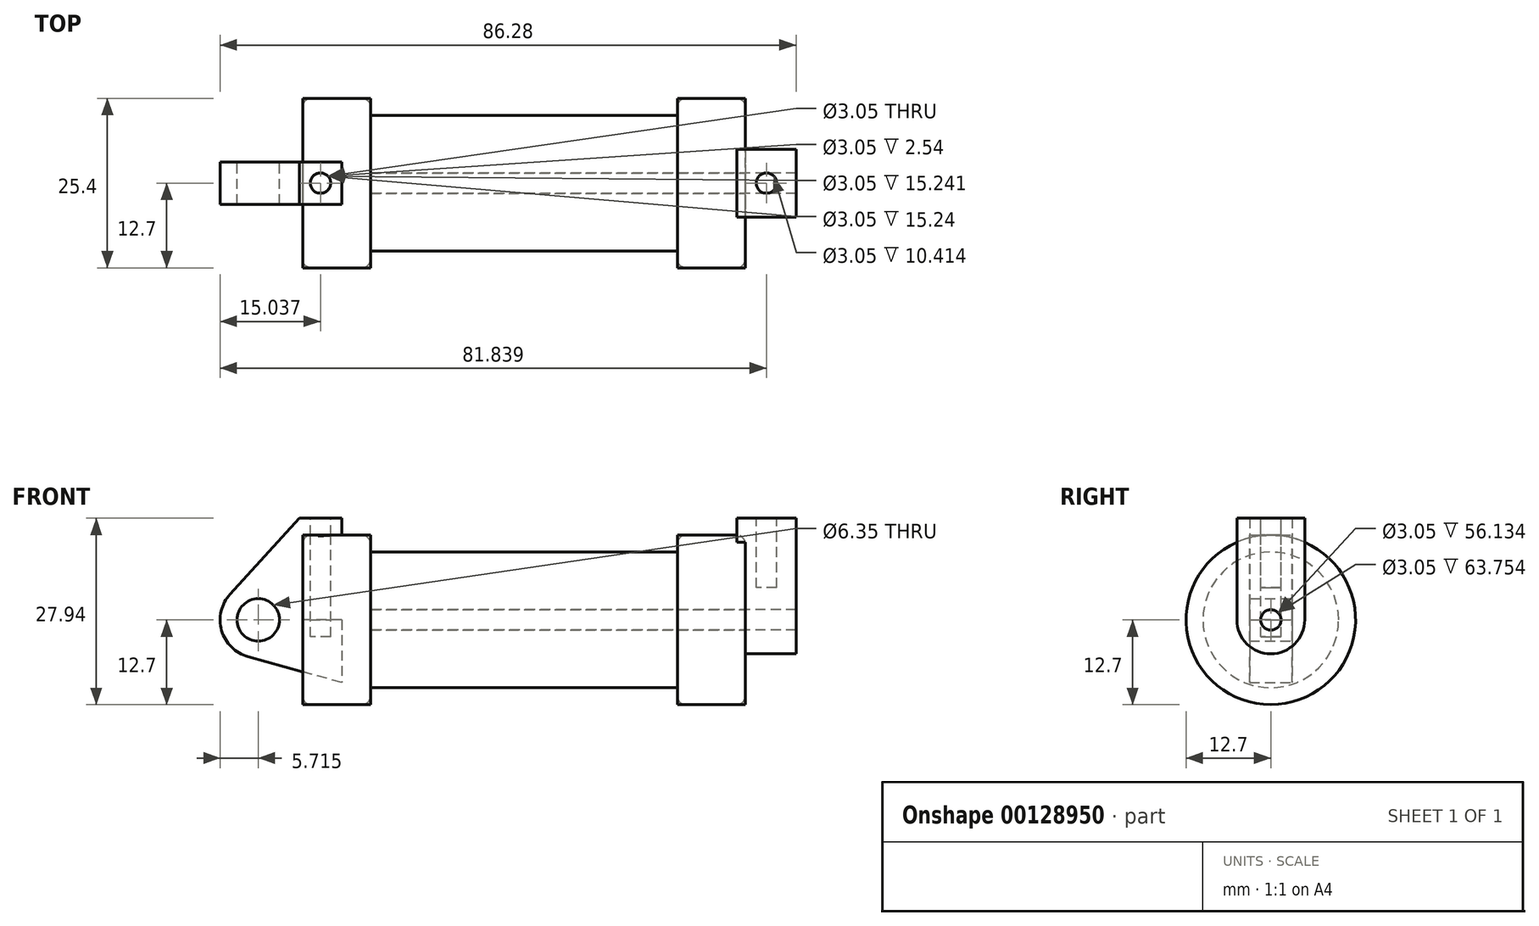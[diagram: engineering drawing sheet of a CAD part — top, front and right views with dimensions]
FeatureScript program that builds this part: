
annotation { "Feature Type Name" : "Feature", "Feature Type Description" : "" }
export const myFeature = defineFeature(function(context is Context, id is Id, definition is map)
    precondition{}
    {
        {
            var Q0;
            Q0=qCreatedBy(makeId("Front.planeOp"),FACE);
            var sketch = newSketch(context, id + "F0", { "sketchPlane" : qUnion([Q0])});
            skLineSegment(sketch, "E0", {"start": v(0, 0) * mm, "end": v(0, 12.7) * mm});
            skLineSegment(sketch, "E1", {"start": v(0, 12.7) * mm, "end": v(10.16, 12.7) * mm});
            skLineSegment(sketch, "E2", {"start": v(10.16, 12.7) * mm, "end": v(10.16, 10.16) * mm});
            skLineSegment(sketch, "E3", {"start": v(10.16, 10.16) * mm, "end": v(56.13, 10.16) * mm});
            skLineSegment(sketch, "E4", {"start": v(56.13, 10.16) * mm, "end": v(56.13, 12.7) * mm});
            skLineSegment(sketch, "E5", {"start": v(56.13, 12.7) * mm, "end": v(66.3, 12.7) * mm});
            skLineSegment(sketch, "E6", {"start": v(66.3, 12.7) * mm, "end": v(66.3, 0) * mm});
            skLineSegment(sketch, "E7", {"start": v(66.3, 0) * mm, "end": v(0, 0) * mm});
            skLineSegment(sketch, "E8", {"start": v(5.84, 15.24) * mm, "end": v(-0.5, 15.24) * mm});
            skLineSegment(sketch, "E9", {"start": v(-0.5, 15.24) * mm, "end": v(-10.88, 3.85) * mm});
            skLineSegment(sketch, "E10", {"start": v(0, 0) * mm, "end": v(-6.65, 0) * mm});
            skCircle(sketch, "E11", {"center": v(-6.65, 0) * mm, "radius": 5.72 * mm});
            skCircle(sketch, "E12", {"center": v(-6.65, 0) * mm, "radius": 3.18 * mm});
            skLineSegment(sketch, "E13", {"start": v(5.84, 15.24) * mm, "end": v(5.84, -9.4) * mm});
            skLineSegment(sketch, "E14", {"start": v(5.84, -9.4) * mm, "end": v(-8.18, -5.5) * mm});
            skSolve(sketch);
        }
        {
            var Q0;
            {var subQ0=sQuery(id+"F0.wireOp",EDGE,"E2");Q0=makeQuery(id+"F0.imprint","IMPRINT",FACE,{"disambiguationData":[TD([[makeQuery(id+"F0.imprint","IMPRINT",EDGE,{"derivedFrom":subQ0}),-1.0]])]});}
            var Q1;
            {var subQ0=sQuery(id+"F0.wireOp",EDGE,"E0");Q1=makeQuery(id+"F0.imprint","IMPRINT",FACE,{"disambiguationData":[TD([[makeQuery(id+"F0.imprint","IMPRINT",EDGE,{"derivedFrom":subQ0}),-1.0]])]});}
            var Q2;
            Q2=sQuery(id+"F0.wireOp",EDGE,"E7");
            revolve(context, id + "F1", {"entities" : qUnion([Q0, Q1]), "axis" : qUnion([Q2]), "revolveType" : RevolveType.FULL});
        }
        {
            var Q0;
            {var subQ3=sQuery(id+"F0.wireOp",EDGE,"E0");Q0=makeQuery(id+"F0.imprint","IMPRINT",FACE,{"disambiguationData":[TD([[makeQuery(id+"F0.imprint","IMPRINT",EDGE,{"derivedFrom":subQ3}),1.0]])]});}
            var Q1;
            {var subQ0=sQuery(id+"F0.wireOp",EDGE,"E14");Q1=makeQuery(id+"F0.imprint","IMPRINT",FACE,{"disambiguationData":[TD([[makeQuery(id+"F0.imprint","IMPRINT",EDGE,{"derivedFrom":subQ0}),-1.0]])]});}
            var Q2;
            {var subQ4=sQuery(id+"F0.wireOp",EDGE,"E12");Q2=makeQuery(id+"F0.imprint","IMPRINT",FACE,{"disambiguationData":[TD([[makeQuery(id+"F0.imprint","IMPRINT",EDGE,{"derivedFrom":subQ4}),-1.0]])]});}
            extrude(context, id + "F2", {"entities" : qUnion([Q0, Q1, Q2]), "endBound" : BoundingType.SYMMETRIC, "depth" : 6.35 * mm});
        }
        {
            var Q0;
            Q0=makeQuery(id+"F1.opRevolve","SWEPT_FACE",FACE,{"disambiguationData":[OSD([sQuery(id+"F0.wireOp",EDGE,"E6")])]});
            var sketch = newSketch(context, id + "F3", { "sketchPlane" : qUnion([Q0])});
            skCircle(sketch, "E15", {"center": v(0, 0) * mm, "radius": 1.52 * mm});
            skCircle(sketch, "E16", {"center": v(0, 0) * mm, "radius": 5.08 * mm});
            skLineSegment(sketch, "E17", {"start": v(5.08, 0) * mm, "end": v(5.08, 15.24) * mm});
            skLineSegment(sketch, "E18", {"start": v(-5.08, 0) * mm, "end": v(-5.08, 15.24) * mm});
            skLineSegment(sketch, "E19", {"start": v(-5.08, 15.24) * mm, "end": v(5.08, 15.24) * mm});
            skSolve(sketch);
        }
        {
            var Q0;
            {var subQ0=sQuery(id+"F3.wireOp",EDGE,"E19");Q0=makeQuery(id+"F3.imprint","IMPRINT",FACE,{"disambiguationData":[TD([[makeQuery(id+"F3.imprint","IMPRINT",EDGE,{"derivedFrom":subQ0}),-1.0]])]});}
            var Q1;
            {var subQ0=sQuery(id+"F3.wireOp",EDGE,"E17");var subQ1=sQuery(id+"F3.wireOp",EDGE,"E16");var subQ2=makeQuery(id+"F3.imprint","INTERSECT",VERTEX,{"derivedFrom":[subQ1,subQ0]});Q1=makeQuery(id+"F3.imprint","IMPRINT",FACE,{"disambiguationData":[TD([[makeQuery(id+"F3.imprint","IMPRINT",EDGE,{"disambiguationData":[TD([[subQ2,-1.0]])],"derivedFrom":subQ1}),-1.0]])]});}
            var Q2;
            Q2=makeQuery(id+"F3.imprint","IMPRINT",FACE,{"disambiguationData":[TD([[makeQuery(id+"F3.imprint","IMPRINT",EDGE,{"derivedFrom":sQuery(id+"F3.wireOp",EDGE,"E15")}),-1.0]])]});
            extrude(context, id + "F4", {"entities" : qUnion([Q0, Q1, Q2]), "operationType" : NewBodyOperationType.ADD, "depth" : 7.62 * mm, "hasSecondDirection" : true, "secondDirectionOppositeDirection" : true, "secondDirectionDepth" : 1.27 * mm});
        }
        {
            var Q0;
            {var subQ0=sQuery(id+"F0.wireOp",EDGE,"E0");Q0=makeQuery(id+"F0.imprint","IMPRINT",FACE,{"disambiguationData":[TD([[makeQuery(id+"F0.imprint","IMPRINT",EDGE,{"derivedFrom":subQ0}),-1.0]])]});}
            var Q1;
            {var subQ0=sQuery(id+"F0.wireOp",EDGE,"E2");Q1=makeQuery(id+"F0.imprint","IMPRINT",FACE,{"disambiguationData":[TD([[makeQuery(id+"F0.imprint","IMPRINT",EDGE,{"derivedFrom":subQ0}),-1.0]])]});}
            var Q2;
            Q2=sQuery(id+"F0.wireOp",EDGE,"E7");
            revolve(context, id + "F5", {"entities" : qUnion([Q0, Q1]), "axis" : qUnion([Q2]), "revolveType" : RevolveType.FULL});
        }
        {
            var Q0;
            Q0=makeQuery(id+"F4.boolean.opBoolean","SPLIT",FACE,{"disambiguationData":[TD([makeQuery(id+"F4.opExtrude","SWEPT_FACE",FACE,{"disambiguationData":[OSD([sQuery(id+"F3.wireOp",EDGE,"E15")])]})])],"derivedFrom":makeQuery(id+"F1.opRevolve","SWEPT_FACE",FACE,{"disambiguationData":[OSD([sQuery(id+"F0.wireOp",EDGE,"E6")])]})});
            var Q1;
            Q1=makeQuery(id+"F1.opRevolve","SWEPT_FACE",FACE,{"disambiguationData":[OSD([sQuery(id+"F0.wireOp",EDGE,"E2")])]});
            extrude(context, id + "F6", {"entities" : qUnion([Q0]), "operationType" : NewBodyOperationType.REMOVE, "endBound" : BoundingType.UP_TO_SURFACE, "oppositeDirection" : true, "endBoundEntityFace" : qUnion([Q1]), "depth" : 25.4 * mm});
        }
        {
            var Q0;
            Q0=makeQuery(id+"F2.opExtrude","SWEPT_FACE",FACE,{"disambiguationData":[OSD([sQuery(id+"F0.wireOp",EDGE,"E8")])]});
            var sketch = newSketch(context, id + "F7", { "sketchPlane" : qUnion([Q0])});
            skCircle(sketch, "E20", {"center": v(2.67, 0) * mm, "radius": 1.52 * mm});
            skPoint(sketch, "E20.centerSnap0", {"position": v(5.84, 0) * mm});
            skPoint(sketch, "E20.centerSnap1", {"position": v(2.67, -3.18) * mm});
            skSolve(sketch);
        }
        {
            var Q0;
            Q0=makeQuery(id+"F4.opExtrude","SWEPT_FACE",FACE,{"disambiguationData":[OSD([sQuery(id+"F3.wireOp",EDGE,"E19")])]});
            var sketch = newSketch(context, id + "F8", { "sketchPlane" : qUnion([Q0])});
            skCircle(sketch, "E21", {"center": v(69.47, 0) * mm, "radius": 1.52 * mm});
            skPoint(sketch, "E21.centerSnap0", {"position": v(65.02, 0) * mm});
            skPoint(sketch, "E21.centerSnap1", {"position": v(69.47, -5.08) * mm});
            skSolve(sketch);
        }
        {
            var Q0;
            Q0=makeQuery(id+"F7.imprint","IMPRINT",FACE,{"disambiguationData":[TD([[makeQuery(id+"F7.imprint","IMPRINT",EDGE,{"derivedFrom":sQuery(id+"F7.wireOp",EDGE,"E20")}),1.0]])]});
            extrude(context, id + "F9", {"entities" : qUnion([Q0]), "operationType" : NewBodyOperationType.REMOVE, "oppositeDirection" : true, "depth" : 17.78 * mm});
        }
        {
            var Q0;
            Q0=makeQuery(id+"F8.imprint","IMPRINT",FACE,{"disambiguationData":[TD([[makeQuery(id+"F8.imprint","IMPRINT",EDGE,{"derivedFrom":sQuery(id+"F8.wireOp",EDGE,"E21")}),1.0]])]});
            extrude(context, id + "F10", {"entities" : qUnion([Q0]), "operationType" : NewBodyOperationType.REMOVE, "oppositeDirection" : true, "depth" : 10.4 * mm});
        }
        {
            var Q0;
            Q0=makeQuery(id+"F1.opRevolve","SWEPT_EDGE",EDGE,{"disambiguationData":[OSD([sQuery(id+"F0.wireOp",EDGE,"E0"),sQuery(id+"F0.wireOp",EDGE,"E1")])]});
            var Q1;
            Q1=makeQuery(id+"F1.opRevolve","SWEPT_EDGE",EDGE,{"disambiguationData":[OSD([sQuery(id+"F0.wireOp",EDGE,"E1"),sQuery(id+"F0.wireOp",EDGE,"E2")])]});
            var Q2;
            Q2=makeQuery(id+"F5.opRevolve","SWEPT_EDGE",EDGE,{"disambiguationData":[OSD([sQuery(id+"F0.wireOp",EDGE,"E5"),sQuery(id+"F0.wireOp",EDGE,"E6")])]});
            var Q3;
            Q3=makeQuery(id+"F5.opRevolve","SWEPT_EDGE",EDGE,{"disambiguationData":[OSD([sQuery(id+"F0.wireOp",EDGE,"E4"),sQuery(id+"F0.wireOp",EDGE,"E5")])]});
            fillet(context, id + "F11", {"entities" : qUnion([Q0, Q1, Q2, Q3]), "radius" : 1.27 * mm, "tangentPropagation" : true, "allowEdgeOverflow" : false});
        }
    });
